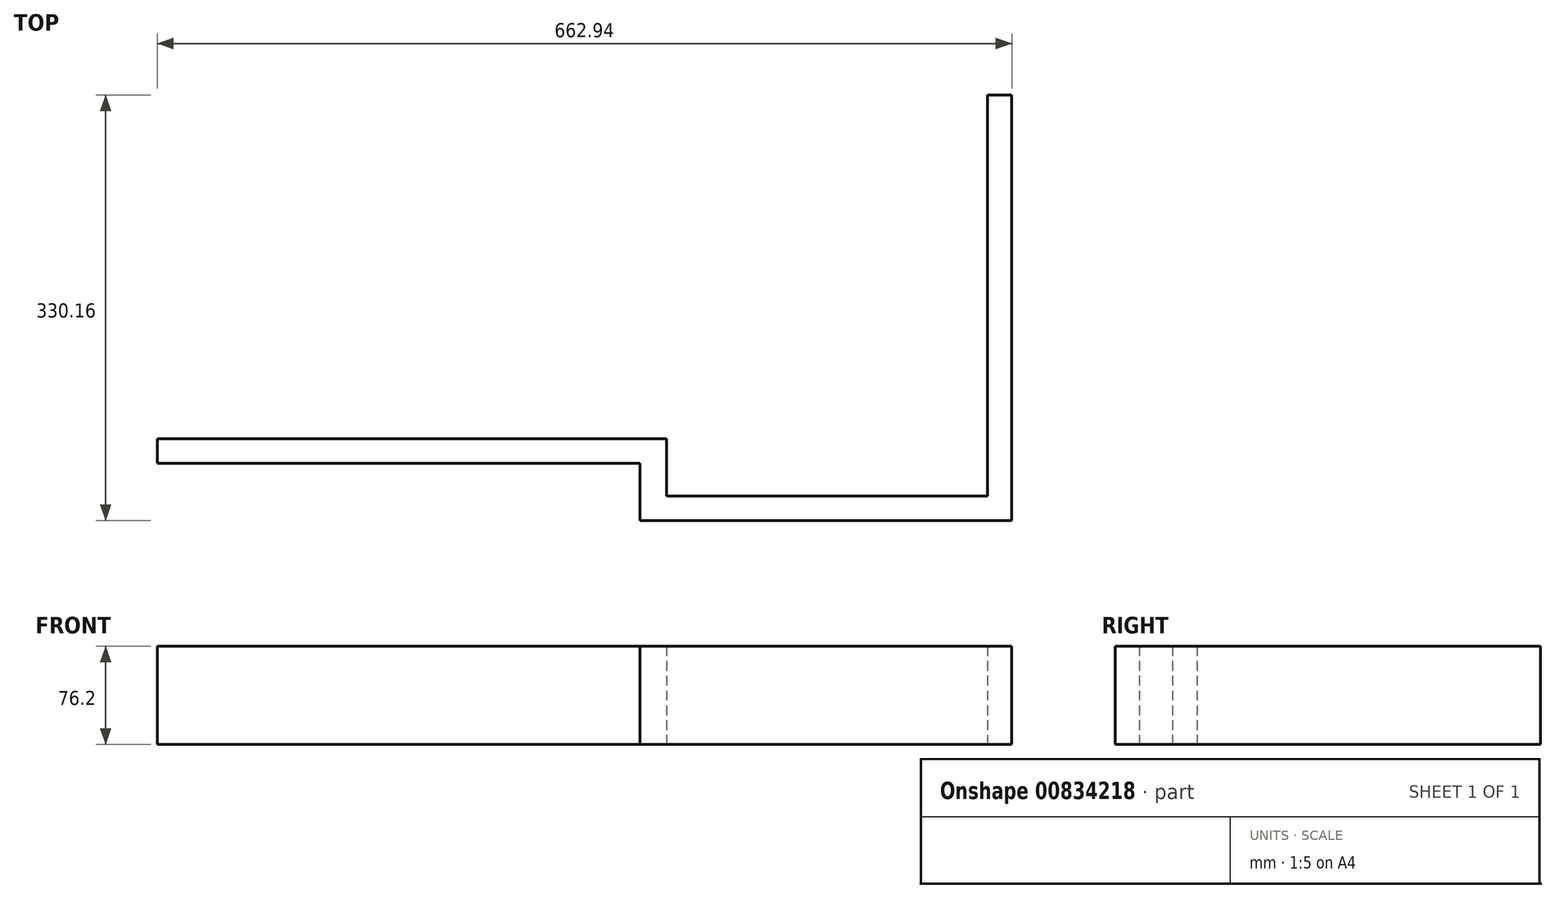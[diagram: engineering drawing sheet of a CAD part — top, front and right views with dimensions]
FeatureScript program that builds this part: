
annotation { "Feature Type Name" : "Feature", "Feature Type Description" : "" }
export const myFeature = defineFeature(function(context is Context, id is Id, definition is map)
    precondition{}
    {
        {
            var Q0;
            Q0=qCreatedBy(makeId("Top.planeOp"),FACE);
            var sketch = newSketch(context, id + "F0", { "sketchPlane" : qUnion([Q0])});
            skLineSegment(sketch, "E0", {"start": v(115.84, 476.6) * mm, "end": v(123.46, 476.6) * mm});
            skLineSegment(sketch, "E1", {"start": v(184.42, -152.04) * mm, "end": v(203.47, -152.04) * mm});
            skPoint(sketch, "E2", {"position": v(-172.45, -437.76) * mm});
            skLineSegment(sketch, "E3", {"start": v(-190.23, -456.84) * mm, "end": v(184.42, -456.84) * mm});
            skLineSegment(sketch, "E4", {"start": v(204.74, -482.28) * mm, "end": v(453.66, -482.28) * mm});
            skLineSegment(sketch, "E5", {"start": v(184.42, -456.84) * mm, "end": v(184.42, -501.3) * mm});
            skLineSegment(sketch, "E6", {"start": v(184.42, -501.3) * mm, "end": v(472.7, -501.3) * mm});
            skPoint(sketch, "E7.right.start.orphan", {"position": v(-44.18, 476.6) * mm});
            skLineSegment(sketch, "E8", {"start": v(-172.45, -437.76) * mm, "end": v(204.74, -437.76) * mm});
            skLineSegment(sketch, "E9", {"start": v(204.74, -437.76) * mm, "end": v(204.74, -482.28) * mm});
            skLineSegment(sketch, "E10", {"start": v(453.66, -482.28) * mm, "end": v(453.66, -171.13) * mm});
            skLineSegment(sketch, "E11", {"start": v(453.66, -171.13) * mm, "end": v(472.7, -171.13) * mm});
            skLineSegment(sketch, "E12", {"start": v(472.7, -171.13) * mm, "end": v(472.7, -501.3) * mm});
            skLineSegment(sketch, "E13", {"start": v(-190.23, -456.84) * mm, "end": v(-190.23, -437.8) * mm});
            skLineSegment(sketch, "E14", {"start": v(-190.23, -437.8) * mm, "end": v(-172.45, -437.76) * mm});
            skSolve(sketch);
        }
        {
            var Q0;
            Q0=makeQuery(id+"F0.imprint","IMPRINT",FACE,{"disambiguationData":[TD([[makeQuery(id+"F0.imprint","IMPRINT",EDGE,{"derivedFrom":sQuery(id+"F0.wireOp",EDGE,"5810cd2c-de9a-4620-bb9c-85d6dd029f4c")}),-1.0]])]});
            var Q1;
            Q1=makeQuery(id+"F0.imprint","IMPRINT",FACE,{"disambiguationData":[TD([[makeQuery(id+"F0.imprint","IMPRINT",EDGE,{"derivedFrom":sQuery(id+"F0.wireOp",EDGE,"E3")}),1.0]])]});
            extrude(context, id + "F1", {"entities" : qUnion([Q0, Q1]), "depth" : 76.2 * mm, "offsetDistance" : 25.4 * mm});
        }
    });
